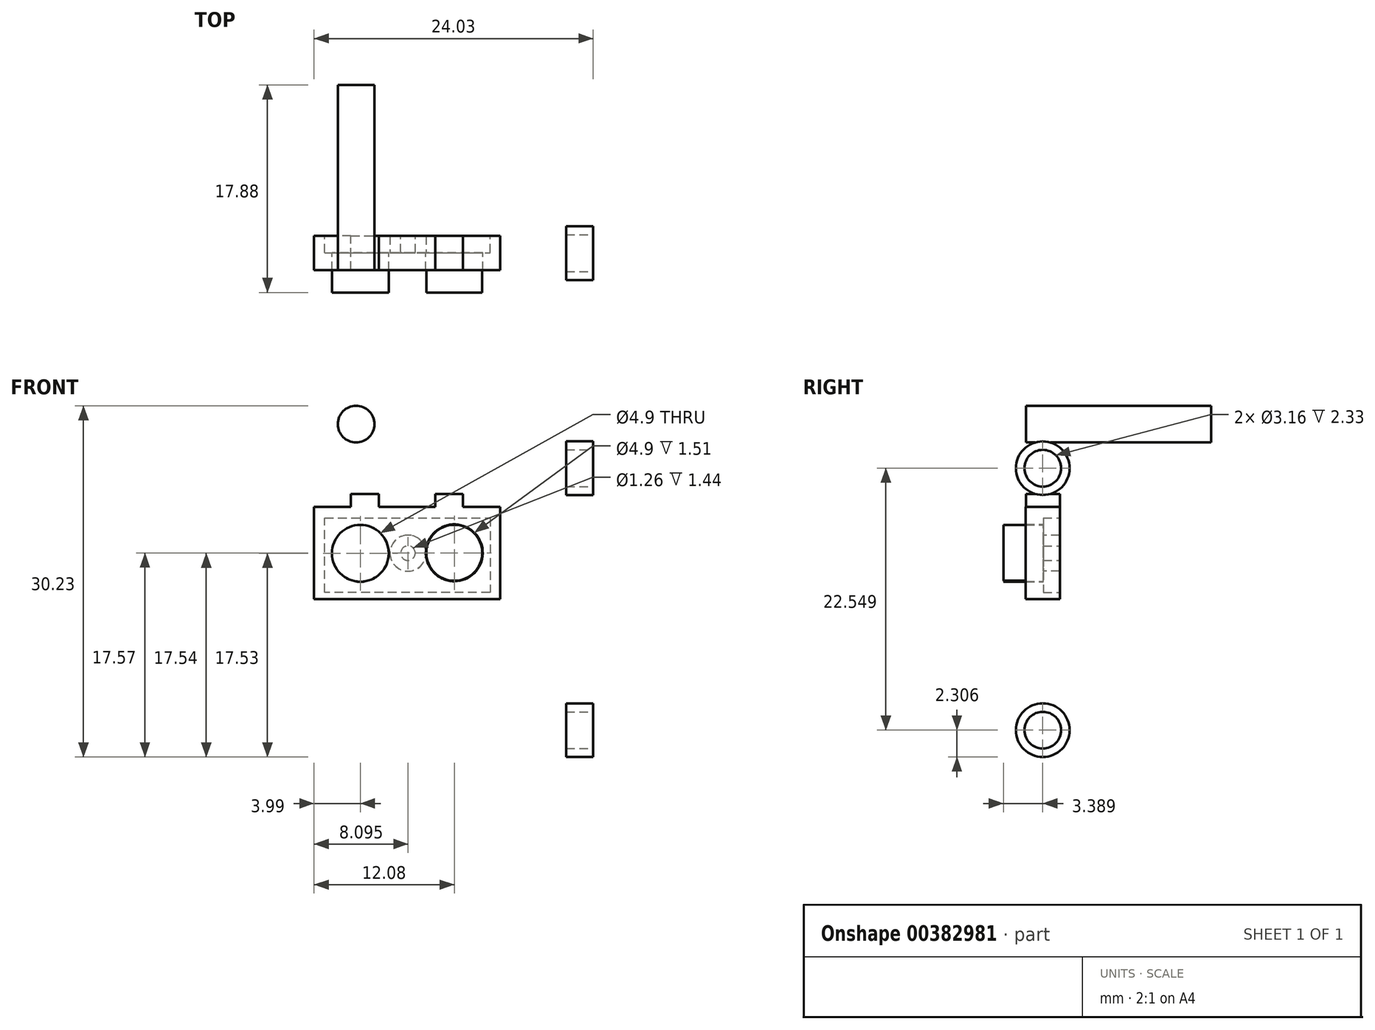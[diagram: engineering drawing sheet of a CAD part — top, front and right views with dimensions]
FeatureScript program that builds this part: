
annotation { "Feature Type Name" : "Feature", "Feature Type Description" : "" }
export const myFeature = defineFeature(function(context is Context, id is Id, definition is map)
    precondition{}
    {
        {
            var Q0;
            Q0=qCreatedBy(makeId("Front.planeOp"),FACE);
            var sketch = newSketch(context, id + "F0", { "sketchPlane" : qUnion([Q0])});
            skLineSegment(sketch, "E0", {"start": v(-8.01, 0) * mm, "end": v(-8.01, 7.94) * mm});
            skLineSegment(sketch, "E1", {"start": v(-8.01, 7.94) * mm, "end": v(-24.03, 7.94) * mm});
            skLineSegment(sketch, "E2", {"start": v(-24.03, 7.94) * mm, "end": v(-24.03, 0) * mm});
            skLineSegment(sketch, "E3", {"start": v(-24.03, 0) * mm, "end": v(-8.01, 0) * mm});
            skCircle(sketch, "E4", {"center": v(-20.04, 3.95) * mm, "radius": 2.45 * mm});
            skCircle(sketch, "E5", {"center": v(-11.95, 4) * mm, "radius": 2.45 * mm});
            skLineSegment(sketch, "E6", {"start": v(-20.85, 7.94) * mm, "end": v(-20.85, 9.07) * mm});
            skLineSegment(sketch, "E7", {"start": v(-20.85, 9.07) * mm, "end": v(-18.44, 9.07) * mm});
            skLineSegment(sketch, "E8", {"start": v(-18.44, 9.07) * mm, "end": v(-18.44, 7.94) * mm});
            skLineSegment(sketch, "E9", {"start": v(-18.44, 7.94) * mm, "end": v(-13.6, 7.94) * mm});
            skLineSegment(sketch, "E10", {"start": v(-13.6, 7.94) * mm, "end": v(-13.6, 9.07) * mm});
            skLineSegment(sketch, "E11", {"start": v(-13.6, 9.07) * mm, "end": v(-11.2, 9.07) * mm});
            skLineSegment(sketch, "E12", {"start": v(-11.2, 9.07) * mm, "end": v(-11.2, 7.94) * mm});
            skSolve(sketch);
        }
        {
            var Q0;
            {var subQ4=sQuery(id+"F0.wireOp",EDGE,"E0");Q0=makeQuery(id+"F0.imprint","IMPRINT",FACE,{"disambiguationData":[TD([[makeQuery(id+"F0.imprint","IMPRINT",EDGE,{"derivedFrom":subQ4}),1.0]])]});}
            extrude(context, id + "F1", {"entities" : qUnion([Q0]), "depth" : 2.96 * mm, "offsetDistance" : 25 * mm});
        }
        {
            var Q0;
            Q0=makeQuery(id+"F1.opExtrude","CAP_FACE",FACE,{"disambiguationData":[OSD([sQuery(id+"F0.wireOp",EDGE,"E0"),sQuery(id+"F0.wireOp",EDGE,"E1"),sQuery(id+"F0.wireOp",EDGE,"E2"),sQuery(id+"F0.wireOp",EDGE,"E3"),sQuery(id+"F0.wireOp",EDGE,"E4"),sQuery(id+"F0.wireOp",EDGE,"E5"),sQuery(id+"F0.wireOp",EDGE,"E9")])],"isStart":false});
            var sketch = newSketch(context, id + "F2", { "sketchPlane" : qUnion([Q0])});
            skCircle(sketch, "E13", {"center": v(-20.04, 3.95) * mm, "radius": 2.45 * mm});
            skCircle(sketch, "E14", {"center": v(-11.95, 4) * mm, "radius": 2.4 * mm});
            skSolve(sketch);
        }
        {
            var Q0;
            Q0=makeQuery(id+"F2.imprint","IMPRINT",FACE,{"disambiguationData":[TD([[makeQuery(id+"F2.imprint","IMPRINT",EDGE,{"derivedFrom":sQuery(id+"F2.wireOp",EDGE,"PouIKoqI-ImN8-zTDx-3qge-Od1ypUP8jgoV")}),1.0]])]});
            var Q1;
            Q1=makeQuery(id+"F2.imprint","IMPRINT",FACE,{"disambiguationData":[TD([[makeQuery(id+"F2.imprint","IMPRINT",EDGE,{"derivedFrom":sQuery(id+"F2.wireOp",EDGE,"E13")}),1.0]])]});
            extrude(context, id + "F3", {"entities" : qUnion([Q0, Q1]), "depth" : 1.92 * mm, "offsetDistance" : 25 * mm});
        }
        {
            var Q0;
            Q0=makeQuery(id+"F1.opExtrude","CAP_FACE",FACE,{"disambiguationData":[OSD([sQuery(id+"F0.wireOp",EDGE,"E0"),sQuery(id+"F0.wireOp",EDGE,"E1"),sQuery(id+"F0.wireOp",EDGE,"E2"),sQuery(id+"F0.wireOp",EDGE,"E3"),sQuery(id+"F0.wireOp",EDGE,"E4"),sQuery(id+"F0.wireOp",EDGE,"E5"),sQuery(id+"F0.wireOp",EDGE,"E9")])],"isStart":false});
            var sketch = newSketch(context, id + "F4", { "sketchPlane" : qUnion([Q0])});
            skCircle(sketch, "E15", {"center": v(-11.95, 4) * mm, "radius": 2.4 * mm});
            skSolve(sketch);
        }
        {
            var Q0;
            Q0=makeQuery(id+"F4.imprint","IMPRINT",FACE,{"disambiguationData":[TD([[makeQuery(id+"F4.imprint","IMPRINT",EDGE,{"derivedFrom":sQuery(id+"F4.wireOp",EDGE,"E15")}),1.0]])]});
            extrude(context, id + "F5", {"entities" : qUnion([Q0]), "depth" : 1.92 * mm, "offsetDistance" : 25 * mm});
        }
        {
            var Q0;
            {var subQ0=sQuery(id+"F0.wireOp",EDGE,"E6");Q0=makeQuery(id+"F0.imprint","IMPRINT",FACE,{"disambiguationData":[TD([[makeQuery(id+"F0.imprint","IMPRINT",EDGE,{"derivedFrom":subQ0}),-1.0]])]});}
            var Q1;
            {var subQ0=sQuery(id+"F0.wireOp",EDGE,"E10");Q1=makeQuery(id+"F0.imprint","IMPRINT",FACE,{"disambiguationData":[TD([[makeQuery(id+"F0.imprint","IMPRINT",EDGE,{"derivedFrom":subQ0}),-1.0]])]});}
            extrude(context, id + "F6", {"entities" : qUnion([Q0, Q1]), "operationType" : NewBodyOperationType.ADD, "depth" : 2.95 * mm, "offsetDistance" : 25 * mm});
        }
        {
            var Q0;
            Q0=qCreatedBy(makeId("Right.planeOp"),FACE);
            var sketch = newSketch(context, id + "F7", { "sketchPlane" : qUnion([Q0])});
            skCircle(sketch, "E16", {"center": v(-1.5, 11.27) * mm, "radius": 2.31 * mm});
            skCircle(sketch, "E17.MirrorC", {"center": v(-1.5, -11.27) * mm, "radius": 2.31 * mm});
            skSolve(sketch);
        }
        {
            var Q0;
            Q0=qSketchRegion(id+"F7",true);
            extrude(context, id + "F8", {"entities" : qUnion([Q0]), "oppositeDirection" : true, "depth" : 2.33 * mm, "offsetDistance" : 25 * mm});
        }
        {
            var Q0;
            {var subQ0=sQuery(id+"F0.wireOp",EDGE,"E1");Q0=makeQuery(id+"F6.boolean.opBoolean","MERGE",FACE,{"derivedFrom":[makeQuery(id+"F1.opExtrude","CAP_FACE",FACE,{"disambiguationData":[OSD([sQuery(id+"F0.wireOp",EDGE,"E0"),subQ0,sQuery(id+"F0.wireOp",EDGE,"E2"),sQuery(id+"F0.wireOp",EDGE,"E3"),sQuery(id+"F0.wireOp",EDGE,"E4"),sQuery(id+"F0.wireOp",EDGE,"E5"),sQuery(id+"F0.wireOp",EDGE,"E9")])],"isStart":true}),makeQuery(id+"F6.opExtrude","CAP_FACE",FACE,{"disambiguationData":[OSD([subQ0,sQuery(id+"F0.wireOp",EDGE,"E10"),sQuery(id+"F0.wireOp",EDGE,"E11"),sQuery(id+"F0.wireOp",EDGE,"E12")])],"isStart":true}),makeQuery(id+"F6.opExtrude","CAP_FACE",FACE,{"disambiguationData":[OSD([subQ0,sQuery(id+"F0.wireOp",EDGE,"E6"),sQuery(id+"F0.wireOp",EDGE,"E7"),sQuery(id+"F0.wireOp",EDGE,"E8")])],"isStart":true})]});}
            var sketch = newSketch(context, id + "F9", { "sketchPlane" : qUnion([Q0])});
            skLineSegment(sketch, "E18", {"start": v(8.87, 7) * mm, "end": v(8.87, 0.6) * mm});
            skLineSegment(sketch, "E19", {"start": v(8.87, 0.6) * mm, "end": v(23.11, 0.6) * mm});
            skLineSegment(sketch, "E20", {"start": v(23.11, 0.6) * mm, "end": v(23.11, 7) * mm});
            skLineSegment(sketch, "E21", {"start": v(23.11, 7) * mm, "end": v(8.87, 7) * mm});
            skSolve(sketch);
        }
        {
            var Q0;
            Q0=makeQuery(id+"F9.imprint","IMPRINT",FACE,{"disambiguationData":[TD([[makeQuery(id+"F9.imprint","IMPRINT",EDGE,{"derivedFrom":sQuery(id+"F9.wireOp",EDGE,"E18")}),1.0]])]});
            extrude(context, id + "F10", {"entities" : qUnion([Q0]), "operationType" : NewBodyOperationType.REMOVE, "oppositeDirection" : true, "depth" : 1.45 * mm, "offsetDistance" : 25 * mm});
        }
        {
            var Q0;
            Q0=makeQuery(id+"F10.boolean.opBoolean","COPY",FACE,{"derivedFrom":makeQuery(id+"F10.opExtrude","CAP_FACE",FACE,{"disambiguationData":[OSD([sQuery(id+"F0.wireOp",EDGE,"E4"),sQuery(id+"F0.wireOp",EDGE,"E5"),sQuery(id+"F9.wireOp",EDGE,"E18"),sQuery(id+"F9.wireOp",EDGE,"E19"),sQuery(id+"F9.wireOp",EDGE,"E20"),sQuery(id+"F9.wireOp",EDGE,"E21")])],"isStart":false})});
            var sketch = newSketch(context, id + "F11", { "sketchPlane" : qUnion([Q0])});
            skCircle(sketch, "E22", {"center": v(15.94, 3.96) * mm, "radius": 1.55 * mm});
            skSolve(sketch);
        }
        {
            var Q0;
            Q0=qSketchRegion(id+"F11",true);
            extrude(context, id + "F12", {"entities" : qUnion([Q0]), "operationType" : NewBodyOperationType.ADD, "depth" : 1.44 * mm, "offsetDistance" : 25 * mm});
        }
        {
            var Q0;
            Q0=makeQuery(id+"F12.opExtrude","CAP_FACE",FACE,{"disambiguationData":[OSD([sQuery(id+"F11.wireOp",EDGE,"E22")])],"isStart":false});
            var sketch = newSketch(context, id + "F13", { "sketchPlane" : qUnion([Q0])});
            skCircle(sketch, "E23", {"center": v(15.94, 3.96) * mm, "radius": 0.63 * mm});
            skSolve(sketch);
        }
        {
            var Q0;
            Q0=makeQuery(id+"F13.imprint","IMPRINT",FACE,{"disambiguationData":[TD([[makeQuery(id+"F13.imprint","IMPRINT",EDGE,{"derivedFrom":sQuery(id+"F13.wireOp",EDGE,"E23")}),1.0]])]});
            extrude(context, id + "F14", {"entities" : qUnion([Q0]), "operationType" : NewBodyOperationType.REMOVE, "oppositeDirection" : true, "depth" : 1.44 * mm, "offsetDistance" : 25 * mm});
        }
        {
            var Q0;
            Q0=makeQuery(id+"F8.opExtrude","CAP_FACE",FACE,{"disambiguationData":[OSD([sQuery(id+"F7.wireOp",EDGE,"E16")])],"isStart":true});
            var sketch = newSketch(context, id + "F15", { "sketchPlane" : qUnion([Q0])});
            skCircle(sketch, "E24", {"center": v(-1.5, 11.27) * mm, "radius": 1.58 * mm});
            skSolve(sketch);
        }
        {
            var Q0;
            Q0=makeQuery(id+"F15.imprint","IMPRINT",FACE,{"disambiguationData":[TD([[makeQuery(id+"F15.imprint","IMPRINT",EDGE,{"derivedFrom":sQuery(id+"F15.wireOp",EDGE,"E24")}),1.0]])]});
            extrude(context, id + "F16", {"entities" : qUnion([Q0]), "operationType" : NewBodyOperationType.REMOVE, "oppositeDirection" : true, "depth" : 25 * mm, "offsetDistance" : 25 * mm});
        }
        {
            var Q0;
            Q0=makeQuery(id+"F8.opExtrude","CAP_FACE",FACE,{"disambiguationData":[OSD([sQuery(id+"F7.wireOp",EDGE,"E17.MirrorC")])],"isStart":true});
            var sketch = newSketch(context, id + "F17", { "sketchPlane" : qUnion([Q0])});
            skCircle(sketch, "E25", {"center": v(-1.5, -11.27) * mm, "radius": 1.58 * mm});
            skSolve(sketch);
        }
        {
            var Q0;
            Q0=makeQuery(id+"F17.imprint","IMPRINT",FACE,{"disambiguationData":[TD([[makeQuery(id+"F17.imprint","IMPRINT",EDGE,{"derivedFrom":sQuery(id+"F17.wireOp",EDGE,"E25")}),1.0]])]});
            extrude(context, id + "F18", {"entities" : qUnion([Q0]), "operationType" : NewBodyOperationType.REMOVE, "oppositeDirection" : true, "depth" : 25 * mm, "offsetDistance" : 25 * mm});
        }
        {
            var Q0;
            Q0=makeQuery(id+"F6.opExtrude","CAP_FACE",FACE,{"disambiguationData":[OSD([sQuery(id+"F0.wireOp",EDGE,"E1"),sQuery(id+"F0.wireOp",EDGE,"E6"),sQuery(id+"F0.wireOp",EDGE,"E7"),sQuery(id+"F0.wireOp",EDGE,"E8")])],"isStart":false});
            var sketch = newSketch(context, id + "F19", { "sketchPlane" : qUnion([Q0])});
            skCircle(sketch, "E26", {"center": v(-20.4, 15.07) * mm, "radius": 1.58 * mm});
            skSolve(sketch);
        }
        {
            var Q0;
            Q0=makeQuery(id+"F19.imprint","IMPRINT",FACE,{"disambiguationData":[TD([[makeQuery(id+"F19.imprint","IMPRINT",EDGE,{"derivedFrom":sQuery(id+"F19.wireOp",EDGE,"E26")}),1.0]])]});
            extrude(context, id + "F20", {"entities" : qUnion([Q0]), "oppositeDirection" : true, "depth" : 15.95 * mm, "offsetDistance" : 25 * mm});
        }
    });
